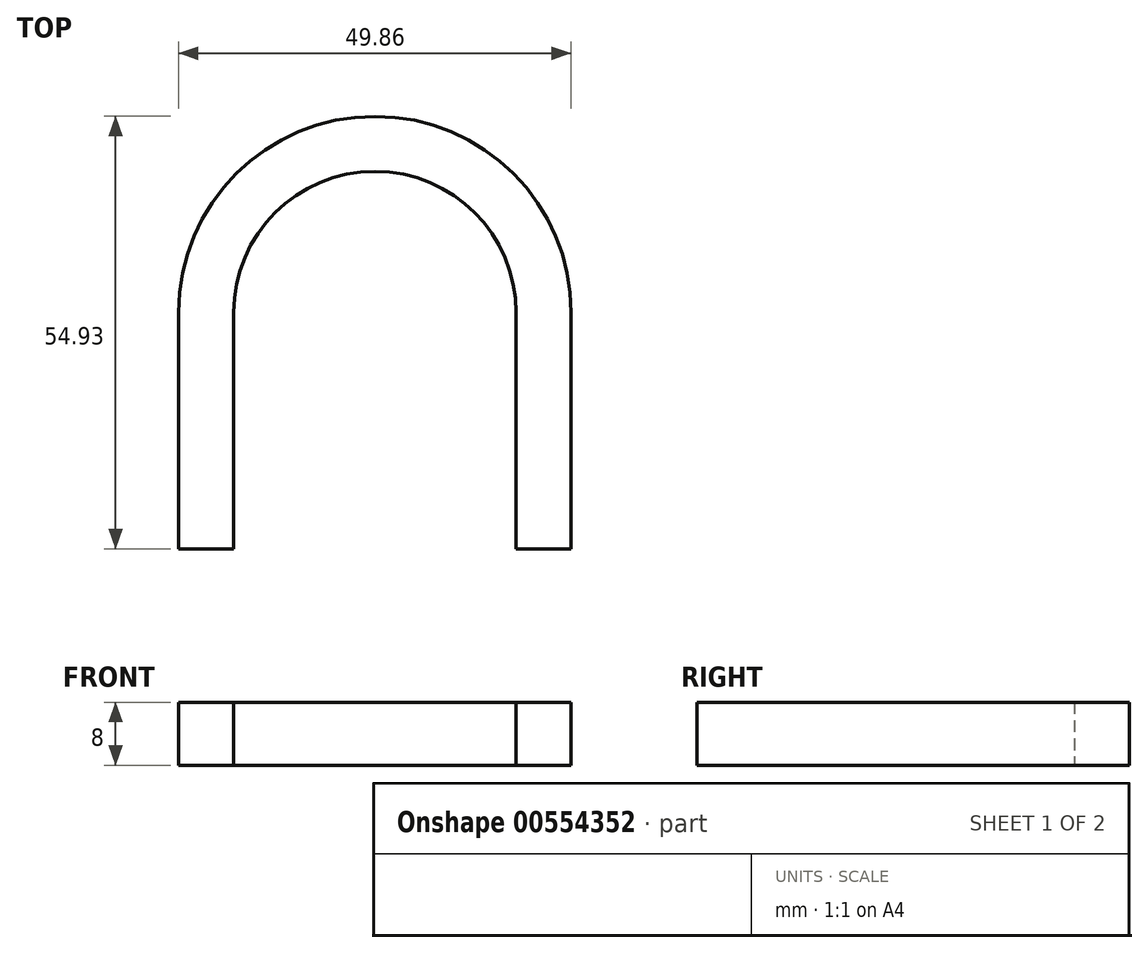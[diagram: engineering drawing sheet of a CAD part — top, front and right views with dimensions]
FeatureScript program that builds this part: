
annotation { "Feature Type Name" : "Feature", "Feature Type Description" : "" }
export const myFeature = defineFeature(function(context is Context, id is Id, definition is map)
    precondition{}
    {
        {
            var Q0;
            Q0=qCreatedBy(makeId("Top.planeOp"),FACE);
            var sketch = newSketch(context, id + "F0", { "sketchPlane" : qUnion([Q0])});
            skLineSegment(sketch, "E0", {"start": v(-135.11, -92.88) * mm, "end": v(-135.11, -62.88) * mm});
            skLineSegment(sketch, "E1", {"start": v(-85.25, -92.88) * mm, "end": v(-85.25, -62.88) * mm});
            skArc(sketch, "E2", {"start": v(-85.25, -62.88) * mm, "mid": v(-110.18, -37.95) * mm, "end": v(-135.11, -62.88) * mm});
            skLineSegment(sketch, "E3.0", {"start": v(-92.25, -92.88) * mm, "end": v(-92.25, -62.88) * mm});
            skArc(sketch, "E3.1", {"start": v(-92.25, -62.88) * mm, "mid": v(-110.18, -44.95) * mm, "end": v(-128.11, -62.88) * mm});
            skLineSegment(sketch, "E3.2", {"start": v(-128.11, -92.88) * mm, "end": v(-128.11, -62.88) * mm});
            skLineSegment(sketch, "E4", {"start": v(-135.11, -92.88) * mm, "end": v(-128.11, -92.88) * mm});
            skLineSegment(sketch, "E5", {"start": v(-92.25, -92.88) * mm, "end": v(-85.25, -92.88) * mm});
            skSolve(sketch);
        }
        {
            var Q0;
            Q0=makeQuery(id+"F0.imprint","IMPRINT",FACE,{"disambiguationData":[TD([[makeQuery(id+"F0.imprint","IMPRINT",EDGE,{"derivedFrom":sQuery(id+"F0.wireOp",EDGE,"E0")}),-1.0]])]});
            extrude(context, id + "F1", {"entities" : qUnion([Q0]), "depth" : 8 * mm, "offsetDistance" : 25 * mm});
        }
    });
